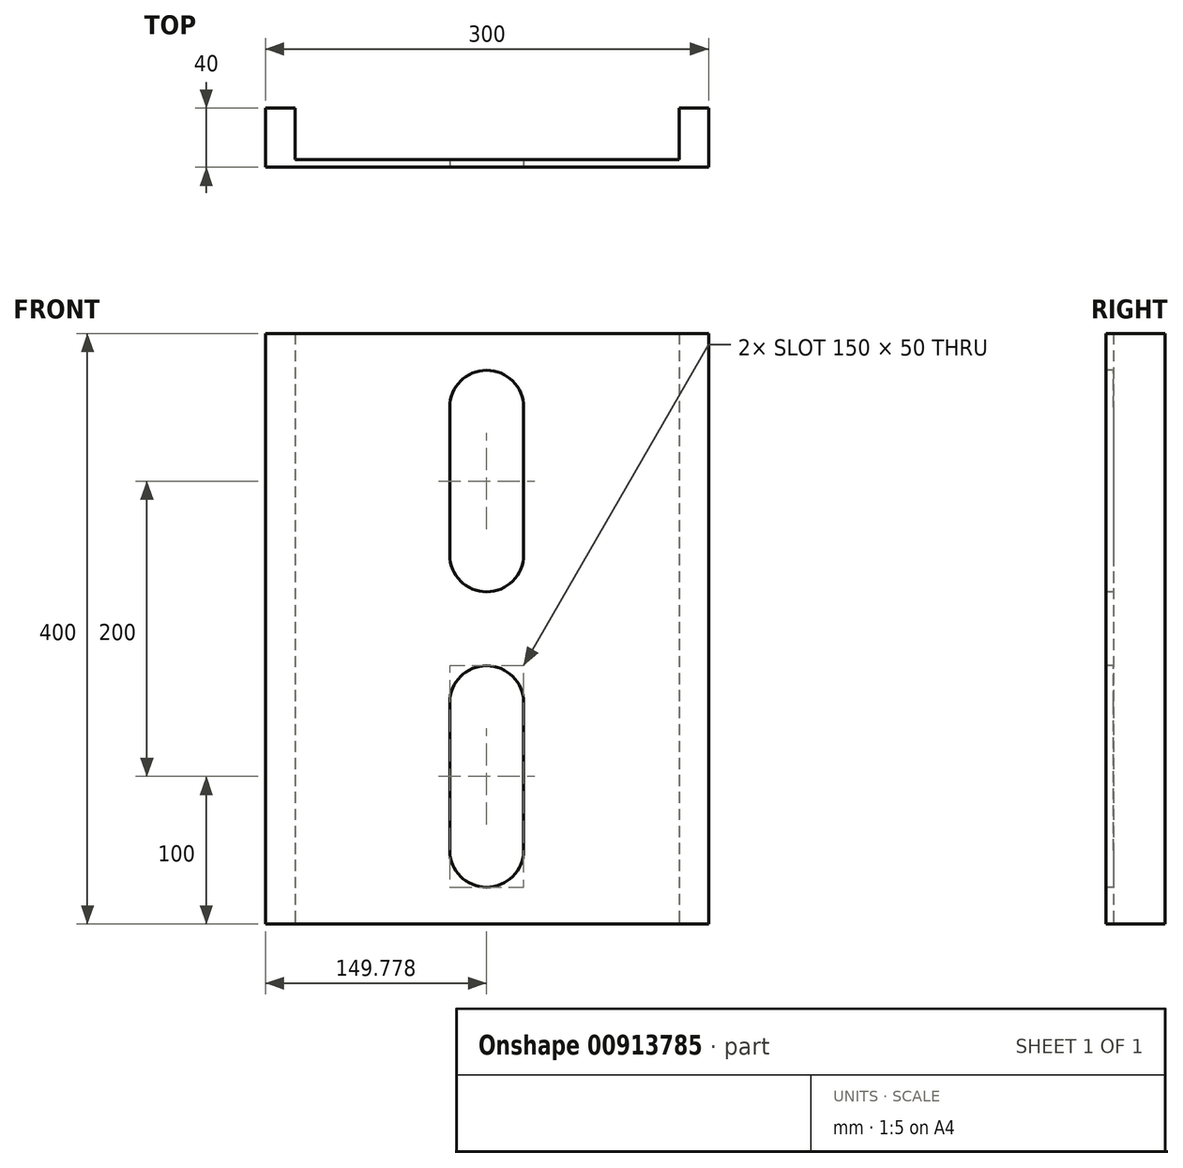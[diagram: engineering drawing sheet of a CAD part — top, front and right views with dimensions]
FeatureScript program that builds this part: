
annotation { "Feature Type Name" : "Feature", "Feature Type Description" : "" }
export const myFeature = defineFeature(function(context is Context, id is Id, definition is map)
    precondition{}
    {
        {
            var Q0;
            Q0=qCreatedBy(makeId("Top.planeOp"),FACE);
            var sketch = newSketch(context, id + "F0", { "sketchPlane" : qUnion([Q0])});
            skLineSegment(sketch, "E0.bottom", {"start": v(-150, -20) * mm, "end": v(150, -20) * mm});
            skLineSegment(sketch, "E0.top", {"start": v(-150, 20) * mm, "end": v(-130, 20) * mm});
            skLineSegment(sketch, "E0.left", {"start": v(-150, -20) * mm, "end": v(-150, 20) * mm});
            skLineSegment(sketch, "E0.right", {"start": v(150, -20) * mm, "end": v(150, 20) * mm});
            skPoint(sketch, "E0.middle", {"position": v(0, 0) * mm});
            skLineSegment(sketch, "E1.bottom", {"start": v(-130, -15) * mm, "end": v(130, -15) * mm});
            skLineSegment(sketch, "E1.left", {"start": v(-130, -15) * mm, "end": v(-130, 20) * mm});
            skLineSegment(sketch, "E1.right", {"start": v(130, -15) * mm, "end": v(130, 20) * mm});
            skPoint(sketch, "E1.middle", {"position": v(0, 2.5) * mm});
            skLineSegment(sketch, "E2.trimOffspring", {"start": v(130, 20) * mm, "end": v(150, 20) * mm});
            skSolve(sketch);
        }
        {
            var Q0;
            Q0=makeQuery(id+"F0.imprint","IMPRINT",FACE,{"disambiguationData":[TD([[makeQuery(id+"F0.imprint","IMPRINT",EDGE,{"derivedFrom":sQuery(id+"F0.wireOp",EDGE,"E0.bottom")}),1.0]])]});
            extrude(context, id + "F1", {"entities" : qUnion([Q0]), "depth" : 400 * mm, "offsetDistance" : 25 * mm});
        }
        {
            var Q0;
            Q0=makeQuery(id+"F1.opExtrude","SWEPT_FACE",FACE,{"disambiguationData":[OSD([sQuery(id+"F0.wireOp",EDGE,"E0.bottom")])]});
            var sketch = newSketch(context, id + "F2", { "sketchPlane" : qUnion([Q0])});
            skLineSegment(sketch, "E3.left", {"start": v(-25.22, 250) * mm, "end": v(-25.22, 350) * mm});
            skLineSegment(sketch, "E3.right", {"start": v(24.78, 250) * mm, "end": v(24.78, 350) * mm});
            skPoint(sketch, "E3.middle", {"position": v(-0.22, 300) * mm});
            skArc(sketch, "E4", {"start": v(-25.22, 350) * mm, "mid": v(-0.22, 375) * mm, "end": v(24.78, 350) * mm});
            skArc(sketch, "E5", {"start": v(24.78, 250) * mm, "mid": v(-0.22, 225) * mm, "end": v(-25.22, 250) * mm});
            skLineSegment(sketch, "E6", {"start": v(-151.6, 200) * mm, "end": v(155.6, 200) * mm, "construction": true});
            skLineSegment(sketch, "E7.MirrorCS", {"start": v(24.78, 150) * mm, "end": v(24.78, 50) * mm});
            skLineSegment(sketch, "E8.MirrorCS", {"start": v(-25.22, 150) * mm, "end": v(-25.22, 50) * mm});
            skArc(sketch, "E9.MirrorCS", {"start": v(-25.22, 50) * mm, "mid": v(-0.22, 25) * mm, "end": v(24.78, 50) * mm});
            skArc(sketch, "E10.MirrorCS", {"start": v(24.78, 150) * mm, "mid": v(-0.22, 175) * mm, "end": v(-25.22, 150) * mm});
            skSolve(sketch);
        }
        {
            var Q0;
            Q0 = qSketchRegion(id + "F2", true);
            extrude(context, id + "F3", {"entities" : qUnion([Q0]), "operationType" : NewBodyOperationType.REMOVE, "oppositeDirection" : true, "depth" : 25 * mm, "offsetDistance" : 25 * mm});
        }
    });
